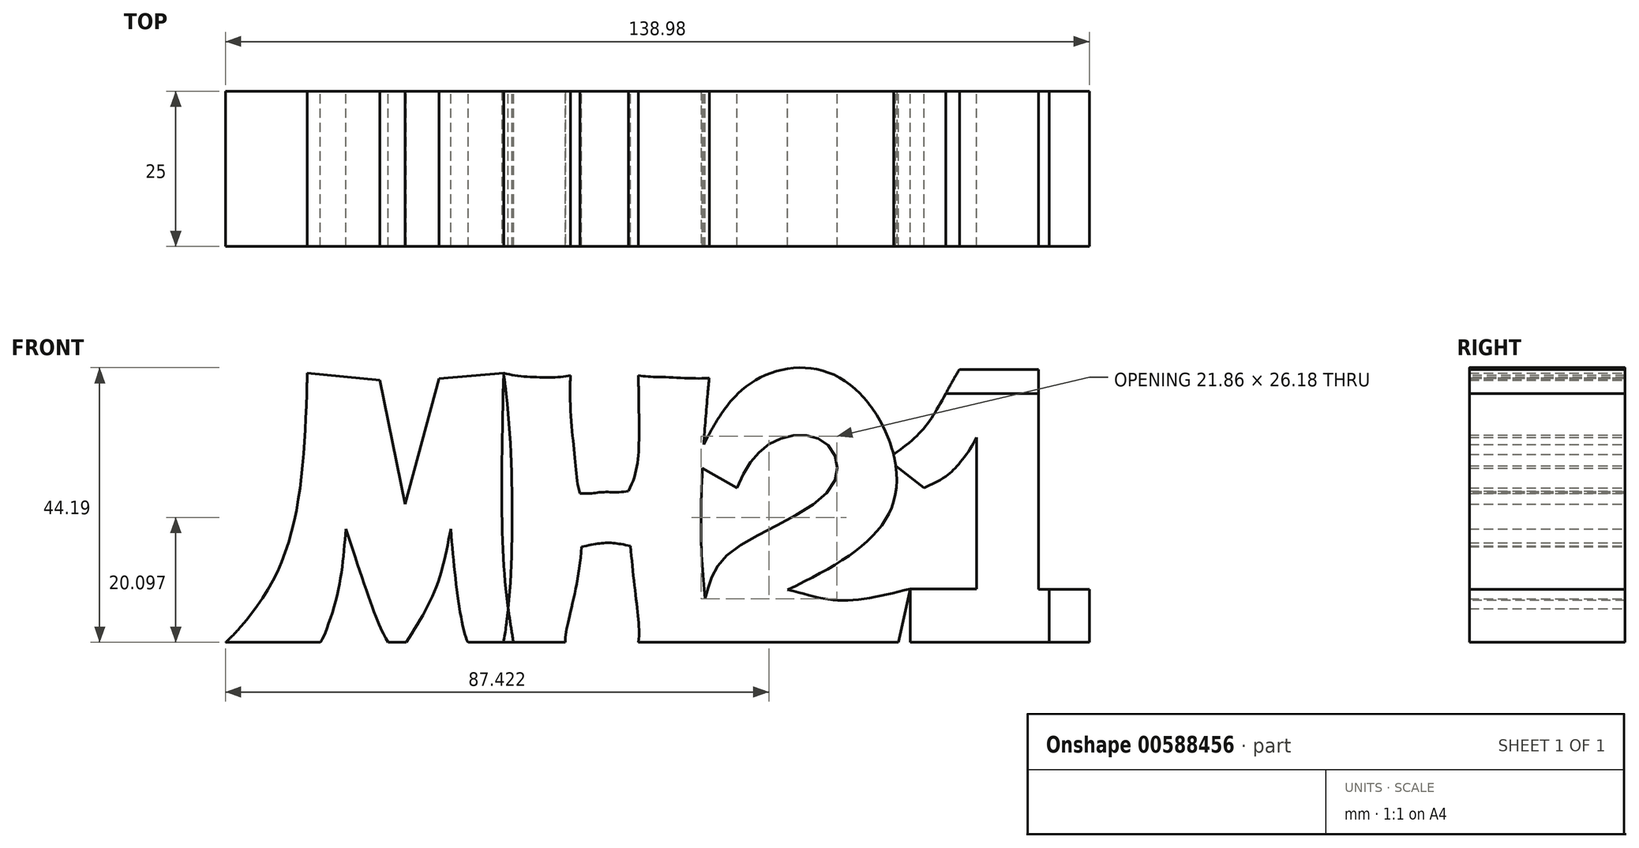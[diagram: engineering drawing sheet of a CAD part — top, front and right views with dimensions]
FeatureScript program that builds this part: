
annotation { "Feature Type Name" : "Feature", "Feature Type Description" : "" }
export const myFeature = defineFeature(function(context is Context, id is Id, definition is map)
    precondition{}
    {
        {
            var Q0;
            Q0=qCreatedBy(makeId("Front.planeOp"),FACE);
            var sketch = newSketch(context, id + "F0", { "sketchPlane" : qUnion([Q0])});
            skLineSegment(sketch, "E0.bottom", {"start": v(-63.91, 40) * mm, "end": v(66.09, 40) * mm});
            skLineSegment(sketch, "E0.top", {"start": v(-63.91, 0) * mm, "end": v(66.09, 0) * mm});
            skLineSegment(sketch, "E0.left", {"start": v(-63.91, 40) * mm, "end": v(-63.91, 0) * mm});
            skLineSegment(sketch, "E0.right", {"start": v(66.09, 40) * mm, "end": v(66.09, 0) * mm});
            skFitSpline(sketch, "E1", {"points": [v(-53.28, 43.32) * mm, v(-58.73, 10.06) * mm, v(-66.44, 0) * mm, v(-66.45, 0) * mm], "startDerivative": vector(-1.74, -59.34) * mm, "endDerivative": vector(-0.77, 0.4) * mm});
            skLineSegment(sketch, "E2", {"start": v(-53.28, 43.32) * mm, "end": v(-41.64, 42.17) * mm});
            skLineSegment(sketch, "E3", {"start": v(-41.64, 42.17) * mm, "end": v(-37.52, 22.23) * mm});
            skLineSegment(sketch, "E4", {"start": v(-37.52, 22.23) * mm, "end": v(-32.08, 42.43) * mm});
            skLineSegment(sketch, "E5", {"start": v(-32.08, 42.43) * mm, "end": v(-21.7, 43.32) * mm});
            skFitSpline(sketch, "E6", {"points": [v(-21.7, 43.32) * mm, v(-21.7, 12.8) * mm, v(-20.11, 0) * mm], "startDerivative": vector(-1.23, -55.78) * mm, "endDerivative": vector(4.85, -28.96) * mm});
            skFitSpline(sketch, "E7", {"points": [v(-47.1, 18.25) * mm, v(-48.69, 6.82) * mm, v(-51.21, 0) * mm, v(-51.35, 0) * mm], "startDerivative": vector(-1.6, -21.17) * mm, "endDerivative": vector(-2.07, 1) * mm});
            skFitSpline(sketch, "E8", {"points": [v(-47.1, 18.25) * mm, v(-41.78, 2.96) * mm, v(-40.32, 0) * mm], "startDerivative": vector(8.76, -26.55) * mm, "endDerivative": vector(4.23, -7.55) * mm});
            skFitSpline(sketch, "E9", {"points": [v(-30.21, 18.25) * mm, v(-32.74, 8.41) * mm, v(-37.4, 0) * mm], "startDerivative": vector(-3.85, -20) * mm, "endDerivative": vector(-10.53, -16.48) * mm});
            skFitSpline(sketch, "E10", {"points": [v(-30.21, 18.25) * mm, v(-28.62, 4.42) * mm, v(-27.42, 0) * mm, v(-27.3, 0) * mm], "startDerivative": vector(2.2, -24.73) * mm, "endDerivative": vector(2.17, 0.87) * mm});
            skFitSpline(sketch, "E11", {"points": [v(-21.7, 43.32) * mm, v(-20.33, 19.51) * mm, v(-21.7, 0) * mm], "startDerivative": vector(6.58, -46.56) * mm, "endDerivative": vector(-6.8, -39.98) * mm});
            skFitSpline(sketch, "E12", {"points": [v(-21.7, 43.32) * mm, v(-15.97, 42.65) * mm, v(-10.94, 42.94) * mm], "startDerivative": vector(10.08, -2.81) * mm, "endDerivative": vector(7.95, 1.97) * mm});
            skFitSpline(sketch, "E13", {"points": [v(-10.94, 42.94) * mm, v(-10.28, 30.13) * mm, v(-9.43, 23.97) * mm], "startDerivative": vector(-1.36, -27.32) * mm, "endDerivative": vector(3.7, -11.93) * mm});
            skFitSpline(sketch, "E14", {"points": [v(-9.43, 23.97) * mm, v(-5.81, 24.17) * mm, v(-1.64, 24.33) * mm], "startDerivative": vector(11.33, -0.78) * mm, "endDerivative": vector(8.7, 1.6) * mm});
            skFitSpline(sketch, "E15", {"points": [v(0, 42.94) * mm, v(0, 30.57) * mm, v(-1.64, 24.33) * mm], "startDerivative": vector(0, -29.13) * mm, "endDerivative": vector(-7.9, -14.5) * mm});
            skFitSpline(sketch, "E16", {"points": [v(0, 42.94) * mm, v(4.6, 42.65) * mm, v(11.39, 42.56) * mm], "startDerivative": vector(8.49, -1.56) * mm, "endDerivative": vector(6.72, 1.26) * mm});
            skFitSpline(sketch, "E17", {"points": [v(11.39, 42.56) * mm, v(10.15, 14.58) * mm, v(11.39, 0) * mm], "startDerivative": vector(-4.95, -49.04) * mm, "endDerivative": vector(1.86, -31.34) * mm});
            skFitSpline(sketch, "E18", {"points": [v(-9.18, 15.37) * mm, v(-11.13, 4.06) * mm, v(-11.75, 0) * mm], "startDerivative": vector(-0.95, -19.94) * mm, "endDerivative": vector(0.55, -8.93) * mm});
            skFitSpline(sketch, "E19", {"points": [v(-1.27, 15.5) * mm, v(-0.2, 5.31) * mm, v(0, 0) * mm], "startDerivative": vector(1.33, -18.06) * mm, "endDerivative": vector(-1.47, -11.45) * mm});
            skFitSpline(sketch, "E20", {"points": [v(-9.18, 15.37) * mm, v(-5.06, 16) * mm, v(-1.27, 15.5) * mm], "startDerivative": vector(9.56, 2) * mm, "endDerivative": vector(10.05, -1.98) * mm});
            skLineSegment(sketch, "E21", {"start": v(9, 28.73) * mm, "end": v(15.83, 24.84) * mm});
            skFitSpline(sketch, "E22", {"points": [v(9, 28.73) * mm, v(18.11, 41.74) * mm, v(32.86, 42.28) * mm, v(41.31, 23.64) * mm, v(24.01, 8.48) * mm], "startDerivative": vector(31.57, 65.82) * mm, "endDerivative": vector(-90.68, -43.3) * mm});
            skFitSpline(sketch, "E23", {"points": [v(15.83, 24.84) * mm, v(21.87, 32.35) * mm, v(29.91, 32.22) * mm, v(31.12, 25.11) * mm, v(14.36, 14.11) * mm, v(10.73, 7) * mm], "startDerivative": vector(22.25, 53.48) * mm, "endDerivative": vector(-11.65, -39.72) * mm});
            skFitSpline(sketch, "E24", {"points": [v(24.01, 8.48) * mm, v(32.73, 6.74) * mm, v(43.72, 8.62) * mm], "startDerivative": vector(20.82, -5.32) * mm, "endDerivative": vector(21.82, 5.53) * mm});
            skLineSegment(sketch, "E25", {"start": v(43.72, 8.62) * mm, "end": v(41.85, 0) * mm});
            skLineSegment(sketch, "E26", {"start": v(11.13, 4.38) * mm, "end": v(12.75, 0) * mm});
            skLineSegment(sketch, "E27", {"start": v(39.97, 29.54) * mm, "end": v(45.93, 24.82) * mm});
            skFitSpline(sketch, "E28", {"points": [v(39.97, 29.54) * mm, v(46.9, 35.76) * mm, v(51.64, 43.92) * mm], "startDerivative": vector(20.14, 12.93) * mm, "endDerivative": vector(10.5, 16.93) * mm});
            skLineSegment(sketch, "E29", {"start": v(51.64, 43.92) * mm, "end": v(64.38, 43.92) * mm});
            skFitSpline(sketch, "E30", {"points": [v(45.93, 24.82) * mm, v(51.15, 28.25) * mm, v(54.42, 32.98) * mm], "startDerivative": vector(19.5, 9.05) * mm, "endDerivative": vector(5.36, 11.2) * mm});
            skLineSegment(sketch, "E31", {"start": v(54.42, 32.98) * mm, "end": v(54.42, 8.62) * mm});
            skLineSegment(sketch, "E32", {"start": v(54.42, 8.62) * mm, "end": v(43.72, 8.62) * mm});
            skLineSegment(sketch, "E33", {"start": v(43.72, 8.62) * mm, "end": v(43.72, 0) * mm});
            skLineSegment(sketch, "E34", {"start": v(64.38, 43.92) * mm, "end": v(64.38, 8.5) * mm});
            skLineSegment(sketch, "E35", {"start": v(64.38, 8.5) * mm, "end": v(72.54, 8.5) * mm});
            skLineSegment(sketch, "E36", {"start": v(72.54, 8.5) * mm, "end": v(72.54, 0) * mm});
            skLineSegment(sketch, "E37", {"start": v(72.54, 0) * mm, "end": v(66.09, 0) * mm});
            skLineSegment(sketch, "E38", {"start": v(-66.44, 0) * mm, "end": v(-61.98, 0) * mm});
            skLineSegment(sketch, "E39", {"start": v(-61.98, 0) * mm, "end": v(-61.17, 0) * mm});
            skSolve(sketch);
        }
        {
            var Q0;
            {var subQ5=sQuery(id+"F0.wireOp",EDGE,"E2");Q0=makeQuery(id+"F0.imprint","IMPRINT",FACE,{"disambiguationData":[TD([[makeQuery(id+"F0.imprint","IMPRINT",EDGE,{"derivedFrom":subQ5}),-1.0]])]});}
            var Q1;
            {var subQ0=sQuery(id+"F0.wireOp",EDGE,"E38");var subQ1=sQuery(id+"F0.wireOp",EDGE,"E0.left");var subQ2=makeQuery(id+"F0.imprint","INTERSECT",VERTEX,{"derivedFrom":[subQ1,subQ0]});Q1=makeQuery(id+"F0.imprint","IMPRINT",FACE,{"disambiguationData":[TD([[makeQuery(id+"F0.imprint","IMPRINT",EDGE,{"disambiguationData":[TD([[subQ2,1.0]])],"derivedFrom":subQ1}),-1.0]])]});}
            var Q2;
            {var subQ23=sQuery(id+"F0.wireOp",EDGE,"E8");Q2=makeQuery(id+"F0.imprint","IMPRINT",FACE,{"disambiguationData":[TD([[makeQuery(id+"F0.imprint","IMPRINT",EDGE,{"derivedFrom":subQ23}),1.0]])]});}
            var Q3;
            {var subQ5=sQuery(id+"F0.wireOp",EDGE,"E5");Q3=makeQuery(id+"F0.imprint","IMPRINT",FACE,{"disambiguationData":[TD([[makeQuery(id+"F0.imprint","IMPRINT",EDGE,{"derivedFrom":subQ5}),-1.0]])]});}
            var Q4;
            {var subQ5=sQuery(id+"F0.wireOp",EDGE,"E12");Q4=makeQuery(id+"F0.imprint","IMPRINT",FACE,{"disambiguationData":[TD([[makeQuery(id+"F0.imprint","IMPRINT",EDGE,{"derivedFrom":subQ5}),-1.0]])]});}
            var Q5;
            {var subQ5=sQuery(id+"F0.wireOp",EDGE,"E16");Q5=makeQuery(id+"F0.imprint","IMPRINT",FACE,{"disambiguationData":[TD([[makeQuery(id+"F0.imprint","IMPRINT",EDGE,{"derivedFrom":subQ5}),-1.0]])]});}
            var Q6;
            {var subQ6=sQuery(id+"F0.wireOp",EDGE,"E14");Q6=makeQuery(id+"F0.imprint","IMPRINT",FACE,{"disambiguationData":[TD([[makeQuery(id+"F0.imprint","IMPRINT",EDGE,{"derivedFrom":subQ6}),-1.0]])]});}
            var Q7;
            {var subQ0=sQuery(id+"F0.wireOp",EDGE,"E22");var subQ1=sQuery(id+"F0.wireOp",EDGE,"E17");var subQ2=makeQuery(id+"F0.imprint","INTERSECT",VERTEX,{"derivedFrom":[subQ1,subQ0]});Q7=makeQuery(id+"F0.imprint","IMPRINT",FACE,{"disambiguationData":[TD([[makeQuery(id+"F0.imprint","IMPRINT",EDGE,{"disambiguationData":[TD([[subQ2,-1.0]])],"derivedFrom":subQ1}),-1.0]])]});}
            var Q8;
            {var subQ0=sQuery(id+"F0.wireOp",EDGE,"E22");var subQ1=sQuery(id+"F0.wireOp",EDGE,"E0.bottom");var subQ2=makeQuery(id+"F0.imprint","INTERSECT",VERTEX,{"disambiguationData":[OD(0.0)],"derivedFrom":[subQ1,subQ0]});Q8=makeQuery(id+"F0.imprint","IMPRINT",FACE,{"disambiguationData":[TD([[makeQuery(id+"F0.imprint","IMPRINT",EDGE,{"disambiguationData":[TD([[subQ2,-1.0]])],"derivedFrom":subQ1}),1.0]])]});}
            var Q9;
            {var subQ0=sQuery(id+"F0.wireOp",EDGE,"E23");Q9=makeQuery(id+"F0.imprint","IMPRINT",FACE,{"disambiguationData":[TD([[makeQuery(id+"F0.imprint","IMPRINT",EDGE,{"derivedFrom":subQ0}),1.0]])]});}
            var Q10;
            {var subQ0=sQuery(id+"F0.wireOp",EDGE,"E28");var subQ1=sQuery(id+"F0.wireOp",EDGE,"E22");var subQ2=makeQuery(id+"F0.imprint","INTERSECT",VERTEX,{"derivedFrom":[subQ1,subQ0]});Q10=makeQuery(id+"F0.imprint","IMPRINT",FACE,{"disambiguationData":[TD([[makeQuery(id+"F0.imprint","IMPRINT",EDGE,{"disambiguationData":[TD([[subQ2,-1.0]])],"derivedFrom":subQ1}),-1.0]])]});}
            var Q11;
            {var subQ5=sQuery(id+"F0.wireOp",EDGE,"E29");Q11=makeQuery(id+"F0.imprint","IMPRINT",FACE,{"disambiguationData":[TD([[makeQuery(id+"F0.imprint","IMPRINT",EDGE,{"derivedFrom":subQ5}),-1.0]])]});}
            var Q12;
            {var subQ4=sQuery(id+"F0.wireOp",EDGE,"E36");Q12=makeQuery(id+"F0.imprint","IMPRINT",FACE,{"disambiguationData":[TD([[makeQuery(id+"F0.imprint","IMPRINT",EDGE,{"derivedFrom":subQ4}),-1.0]])]});}
            extrude(context, id + "F1", {"entities" : qUnion([Q0, Q1, Q2, Q3, Q4, Q5, Q6, Q7, Q8, Q9, Q10, Q11, Q12]), "depth" : 25 * mm, "offsetDistance" : 25 * mm});
        }
        {
            var Q0;
            {var subQ0=sQuery(id+"F0.wireOp",EDGE,"E30");Q0=makeQuery(id+"F0.imprint","IMPRINT",FACE,{"disambiguationData":[TD([[makeQuery(id+"F0.imprint","IMPRINT",EDGE,{"derivedFrom":subQ0}),1.0]])]});}
            var Q1;
            {var subQ0=sQuery(id+"F0.wireOp",EDGE,"E6");var subQ1=sQuery(id+"F0.wireOp",EDGE,"E0.top");var subQ2=makeQuery(id+"F0.imprint","INTERSECT",VERTEX,{"derivedFrom":[subQ1,subQ0]});Q1=makeQuery(id+"F0.imprint","IMPRINT",FACE,{"disambiguationData":[TD([[makeQuery(id+"F0.imprint","IMPRINT",EDGE,{"disambiguationData":[TD([[subQ2,1.0]])],"derivedFrom":subQ1}),1.0]])]});}
            extrude(context, id + "F2", {"entities" : qUnion([Q0, Q1]), "depth" : 25 * mm, "offsetDistance" : 25 * mm});
        }
    });
